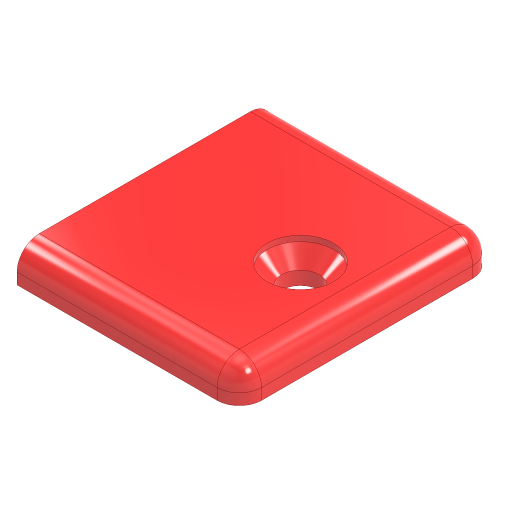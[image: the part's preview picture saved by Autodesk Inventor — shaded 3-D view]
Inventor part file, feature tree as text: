
AUTODESK INVENTOR PART (.ipt)
format: ipt  version: 2024.3 (Build 283343000, 343)  size: 166,912 bytes
history: native  units: mm
features: sketch x3, extrude x2, fillet x2, hole x1, chamfer x1, projected_geometry x1
ambient origin geometry x8: Origin, YZ Plane, XZ Plane, XY Plane, X Axis, Y Axis, Z Axis, Center Point
bodies: Solid1 (feature_tree)
feature tree (10):
  extrude  "Extrusion1"  Depth=23.0mm
  extrude  "Extrusion2"  Depth=20.2mm
  hole  "Hole1"  [1 undecoded]
  chamfer  "Chamfer1"  Distance=6.0mm
  fillet  "Fillet1"  Radius=2.0mm
  fillet  "Fillet2"  Radius=2.0mm
  sketch  "Sketch1"  dims[d0=20.0mm d1=23.0mm]
  sketch  "Sketch2"  dims[d2=3.0mm d3=0.0mm d4=20.2mm]
  projected_geometry  "Projected Loop1"
  sketch  "Sketch3"  dims[d5=10.0mm d6=1.4mm d7=0.0mm d8=6.0mm d9=3.4mm d10=6.0mm d11=6.0mm d12=0.5mm d13=90.0deg d14=8.0mm d15=20.594885mm d16=1.3mm d17=2.0mm d18=45.0deg d19=2.0mm d20=2.0mm]
note: 1 required parameter value undecoded (feature->parameter linkage not recoverable at this tier; creation-order binding heuristic only, values carry confidence <= 0.55)
